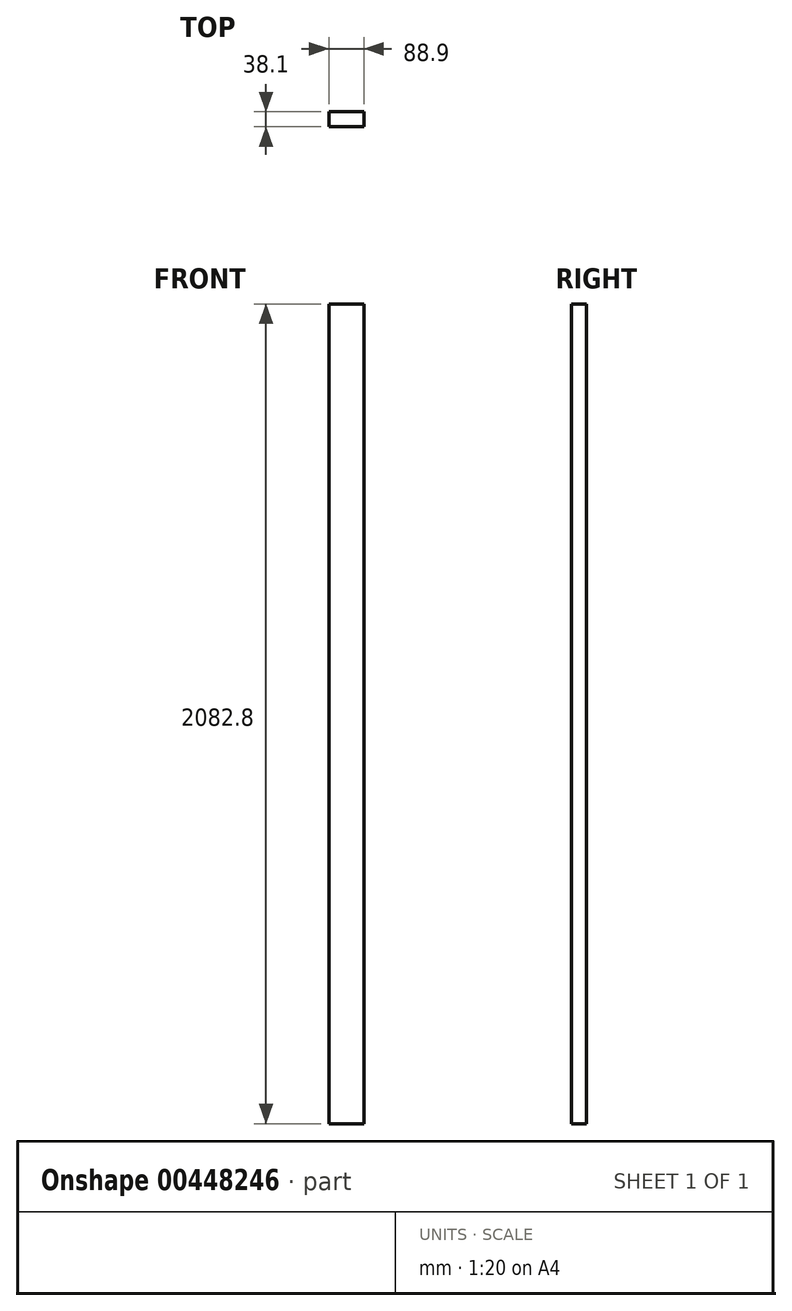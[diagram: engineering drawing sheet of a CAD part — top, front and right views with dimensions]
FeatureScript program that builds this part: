
annotation { "Feature Type Name" : "Feature", "Feature Type Description" : "" }
export const myFeature = defineFeature(function(context is Context, id is Id, definition is map)
    precondition{}
    {
        {
            var Q0;
            Q0=qCreatedBy(makeId("Top.planeOp"),FACE);
            var sketch = newSketch(context, id + "F0", { "sketchPlane" : qUnion([Q0])});
            skLineSegment(sketch, "E0.bottom", {"start": v(-44.45, 19.05) * mm, "end": v(44.45, 19.05) * mm});
            skLineSegment(sketch, "E0.top", {"start": v(-44.45, -19.05) * mm, "end": v(44.45, -19.05) * mm});
            skLineSegment(sketch, "E0.left", {"start": v(-44.45, 19.05) * mm, "end": v(-44.45, -19.05) * mm});
            skLineSegment(sketch, "E0.right", {"start": v(44.45, 19.05) * mm, "end": v(44.45, -19.05) * mm});
            skSolve(sketch);
        }
        {
            var Q0;
            Q0 = qSketchRegion(id + "F0", true);
            extrude(context, id + "F1", {"entities" : qUnion([Q0]), "depth" : 2082.8 * mm});
        }
    });
